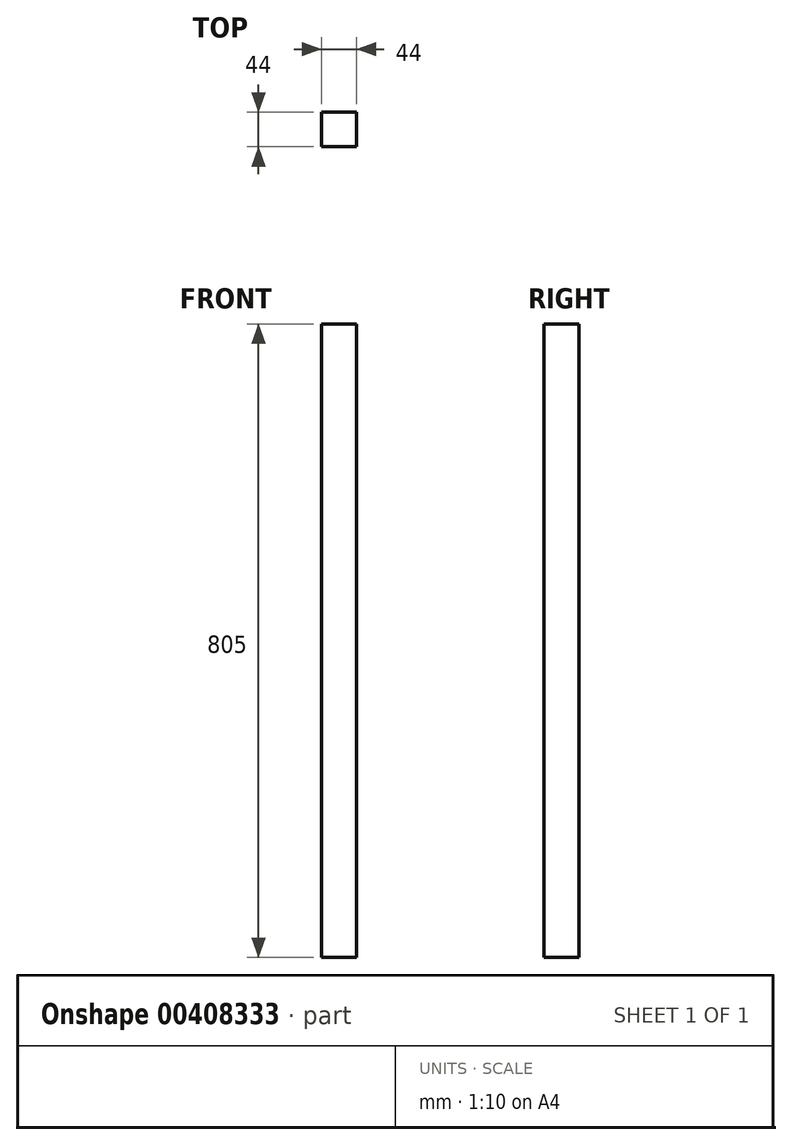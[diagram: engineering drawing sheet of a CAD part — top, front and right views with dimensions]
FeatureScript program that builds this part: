
annotation { "Feature Type Name" : "Feature", "Feature Type Description" : "" }
export const myFeature = defineFeature(function(context is Context, id is Id, definition is map)
    precondition{}
    {
        {
            var Q0;
            Q0=qCreatedBy(makeId("Top.planeOp"),FACE);
            var sketch = newSketch(context, id + "F0", { "sketchPlane" : qUnion([Q0])});
            skLineSegment(sketch, "E0.bottom", {"start": v(22, 22) * mm, "end": v(-22, 22) * mm});
            skLineSegment(sketch, "E0.top", {"start": v(22, -22) * mm, "end": v(-22, -22) * mm});
            skLineSegment(sketch, "E0.left", {"start": v(22, 22) * mm, "end": v(22, -22) * mm});
            skLineSegment(sketch, "E0.right", {"start": v(-22, 22) * mm, "end": v(-22, -22) * mm});
            skPoint(sketch, "E0.middle", {"position": v(0, 0) * mm});
            skSolve(sketch);
        }
        {
            var Q0;
            Q0=makeQuery(id+"F0.imprint","IMPRINT",FACE,{"disambiguationData":[TD([[makeQuery(id+"F0.imprint","IMPRINT",EDGE,{"derivedFrom":sQuery(id+"F0.wireOp",EDGE,"E0.bottom")}),1.0]])]});
            extrude(context, id + "F1", {"entities" : qUnion([Q0]), "depth" : (820 - 15) * mm});
        }
    });
